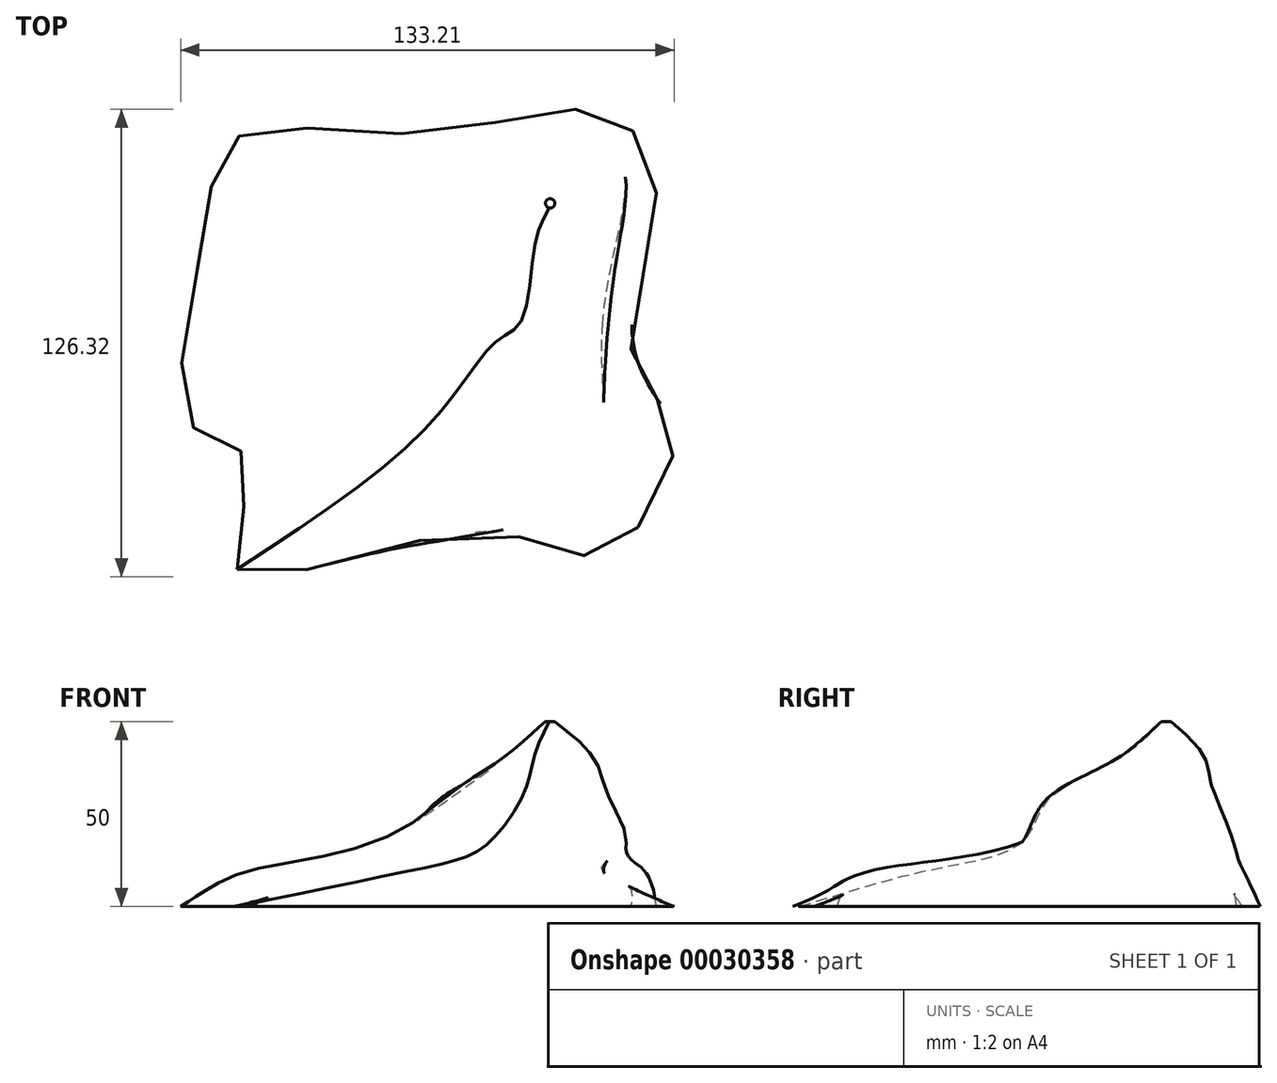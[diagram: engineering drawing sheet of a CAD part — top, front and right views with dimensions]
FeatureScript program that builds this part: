
annotation { "Feature Type Name" : "Feature", "Feature Type Description" : "" }
export const myFeature = defineFeature(function(context is Context, id is Id, definition is map)
    precondition{}
    {
        {
            var Q0;
            Q0=qCreatedBy(makeId("Top.planeOp"),FACE);
            var sketch = newSketch(context, id + "F0", { "sketchPlane" : qUnion([Q0])});
            skFitSpline(sketch, "E0", {"points": [v(-63.96, 23.14) * mm, v(-53.6, 53.83) * mm, v(-3.68, 54.57) * mm, v(44.76, 60.12) * mm, v(59, 36.82) * mm, v(52.53, -6.44) * mm, v(63.62, -26.6) * mm, v(45.5, -58.77) * mm, v(11.66, -53.22) * mm, v(-54.16, -63.2) * mm, v(-51.01, -34.18) * mm, v(-66.36, -24.56) * mm, v(-63.96, 23.14) * mm]});
            skLineSegment(sketch, "E1", {"start": v(-53.6, 53.83) * mm, "end": v(45.5, -58.77) * mm, "construction": true});
            skSolve(sketch);
        }
        {
            var Q0;
            Q0=qCreatedBy(makeId("Top.planeOp"),FACE);
            cPlane(context, id + "F1", {"entities" : qUnion([Q0]), "cplaneType" : CPlaneType.OFFSET, "offset" : 10 * mm, "width" : 150 * mm, "height" : 150 * mm});
        }
        {
            var Q0;
            Q0=qCreatedBy(id+"F1.planeOp",FACE);
            cPlane(context, id + "F2", {"entities" : qUnion([Q0]), "cplaneType" : CPlaneType.OFFSET, "offset" : 10 * mm, "width" : 150 * mm, "height" : 150 * mm});
        }
        {
            var Q0;
            Q0=qCreatedBy(id+"F2.planeOp",FACE);
            cPlane(context, id + "F3", {"entities" : qUnion([Q0]), "cplaneType" : CPlaneType.OFFSET, "offset" : 10 * mm, "width" : 150 * mm, "height" : 150 * mm});
        }
        {
            var Q0;
            Q0=qCreatedBy(id+"F3.planeOp",FACE);
            cPlane(context, id + "F4", {"entities" : qUnion([Q0]), "cplaneType" : CPlaneType.OFFSET, "offset" : 10 * mm, "width" : 150 * mm, "height" : 150 * mm});
        }
        {
            var Q0;
            Q0=qCreatedBy(id+"F4.planeOp",FACE);
            cPlane(context, id + "F5", {"entities" : qUnion([Q0]), "cplaneType" : CPlaneType.OFFSET, "offset" : 10 * mm, "width" : 150 * mm, "height" : 150 * mm});
        }
        {
            var Q0;
            Q0=qCreatedBy(id+"F5.planeOp",FACE);
            cPlane(context, id + "F6", {"entities" : qUnion([Q0]), "cplaneType" : CPlaneType.OFFSET, "offset" : 10 * mm, "width" : 150 * mm, "height" : 150 * mm});
        }
        {
            var Q0;
            Q0=qCreatedBy(id+"F6.planeOp",FACE);
            cPlane(context, id + "F7", {"entities" : qUnion([Q0]), "cplaneType" : CPlaneType.OFFSET, "offset" : 10 * mm, "width" : 150 * mm, "height" : 150 * mm});
        }
        {
            var Q0;
            Q0=qCreatedBy(id+"F1.planeOp",FACE);
            var sketch = newSketch(context, id + "F8", { "sketchPlane" : qUnion([Q0])});
            skFitSpline(sketch, "E2", {"points": [v(-3.29, 49.92) * mm, v(30.18, 56.11) * mm, v(50.5, 52.24) * mm, v(55.14, 37.34) * mm, v(44.7, 0) * mm, v(44.12, -24.19) * mm, v(27.67, -42.57) * mm, v(-22.64, -15.29) * mm, v(-44.7, 5.42) * mm, v(-47.02, 31.93) * mm, v(-3.29, 49.92) * mm]});
            skPoint(sketch, "E3", {"position": v(-36.93, 40) * mm});
            skPoint(sketch, "E4", {"position": v(-5.9, -27.81) * mm});
            skSolve(sketch);
        }
        {
            var Q0;
            Q0=qCreatedBy(id+"F2.planeOp",FACE);
            var sketch = newSketch(context, id + "F9", { "sketchPlane" : qUnion([Q0])});
            skFitSpline(sketch, "E5", {"points": [v(0, 47.02) * mm, v(25.93, 52.82) * mm, v(45.86, 49.15) * mm, v(50.5, 39.47) * mm, v(38.7, 7.35) * mm, v(23.22, 0) * mm, v(-2.32, 0) * mm, v(-11.03, 15.48) * mm, v(-8.9, 36.38) * mm, v(0, 47.02) * mm]});
            skPoint(sketch, "E6", {"position": v(16.39, -1.11) * mm});
            skPoint(sketch, "E7", {"position": v(-8.5, 6.42) * mm});
            skPoint(sketch, "E8", {"position": v(-11.22, 25.4) * mm});
            skSolve(sketch);
        }
        {
            var Q0;
            Q0=qCreatedBy(id+"F3.planeOp",FACE);
            var sketch = newSketch(context, id + "F10", { "sketchPlane" : qUnion([Q0])});
            skFitSpline(sketch, "E9", {"points": [v(2.13, 43.54) * mm, v(15.67, 48.37) * mm, v(33.67, 48.18) * mm, v(44.7, 42.76) * mm, v(43.92, 26.12) * mm, v(34.63, 10.45) * mm, v(17.22, 4.45) * mm, v(2.9, 12.19) * mm, v(4.45, 28.83) * mm, v(2.13, 43.54) * mm]});
            skPoint(sketch, "E10", {"position": v(7.08, 7.5) * mm});
            skPoint(sketch, "E11", {"position": v(23, 4.8) * mm});
            skPoint(sketch, "E12", {"position": v(3.5, 21.4) * mm});
            skSolve(sketch);
        }
        {
            var Q0;
            Q0=qCreatedBy(id+"F4.planeOp",FACE);
            var sketch = newSketch(context, id + "F11", { "sketchPlane" : qUnion([Q0])});
            skFitSpline(sketch, "E13", {"points": [v(21.67, 45.47) * mm, v(33.28, 44.3) * mm, v(39.28, 41.21) * mm, v(40.63, 26.5) * mm, v(22.64, 23.6) * mm, v(17.41, 33.67) * mm, v(21.67, 45.47) * mm]});
            skPoint(sketch, "E14", {"position": v(30.38, 35.4) * mm});
            skPoint(sketch, "E15", {"position": v(34, 22.74) * mm});
            skPoint(sketch, "E16", {"position": v(25.82, 22.61) * mm});
            skPoint(sketch, "E17", {"position": v(18.6, 27.59) * mm});
            skPoint(sketch, "E18", {"position": v(17.83, 38.73) * mm});
            skPoint(sketch, "E19", {"position": v(29.26, 45.44) * mm});
            skSolve(sketch);
        }
        {
            var Q0;
            Q0=qCreatedBy(id+"F5.planeOp",FACE);
            var sketch = newSketch(context, id + "F12", { "sketchPlane" : qUnion([Q0])});
            skCircle(sketch, "E20", {"center": v(30.29, 35.6) * mm, "radius": 1.26 * mm});
            skPoint(sketch, "E21", {"position": v(29.97, 34.38) * mm});
            skSolve(sketch);
        }
        {
            var Q0;
            Q0 = qSketchRegion(id + "F0", true);
            var Q1;
            Q1 = qSketchRegion(id + "F8", true);
            var Q2;
            Q2 = qSketchRegion(id + "F9", true);
            var Q3;
            Q3 = qSketchRegion(id + "F10", true);
            var Q4;
            Q4 = qSketchRegion(id + "F11", true);
            var Q5;
            Q5 = qSketchRegion(id + "F12", true);
            var Q6;
            Q6=sQuery(id+"F0.wireOp",VERTEX,"E0.9.internal");
            var Q7;
            Q7=sQuery(id+"F8.wireOp",VERTEX,"E4");
            var Q8;
            Q8=sQuery(id+"F9.wireOp",VERTEX,"E6");
            var Q9;
            Q9=sQuery(id+"F10.wireOp",VERTEX,"E11");
            var Q10;
            Q10=sQuery(id+"F11.wireOp",VERTEX,"E16");
            var Q11;
            Q11=sQuery(id+"F12.wireOp",VERTEX,"E21");
            loft(context, id + "F13", {"sheetProfilesArray" : [{ "sheetProfileEntities" : qUnion([Q0]) }, { "sheetProfileEntities" : qUnion([Q1]) }, { "sheetProfileEntities" : qUnion([Q2]) }, { "sheetProfileEntities" : qUnion([Q3]) }, { "sheetProfileEntities" : qUnion([Q4]) }, { "sheetProfileEntities" : qUnion([Q5]) }], "matchConnections" : true, "connections" : [{ "connectionEntities" : qUnion([Q6, Q7, Q8, Q9, Q10, Q11]), "connectionEdgeQueries" : qUnion([]), "connectionEdgeParameters" : [] }]});
        }
    });
